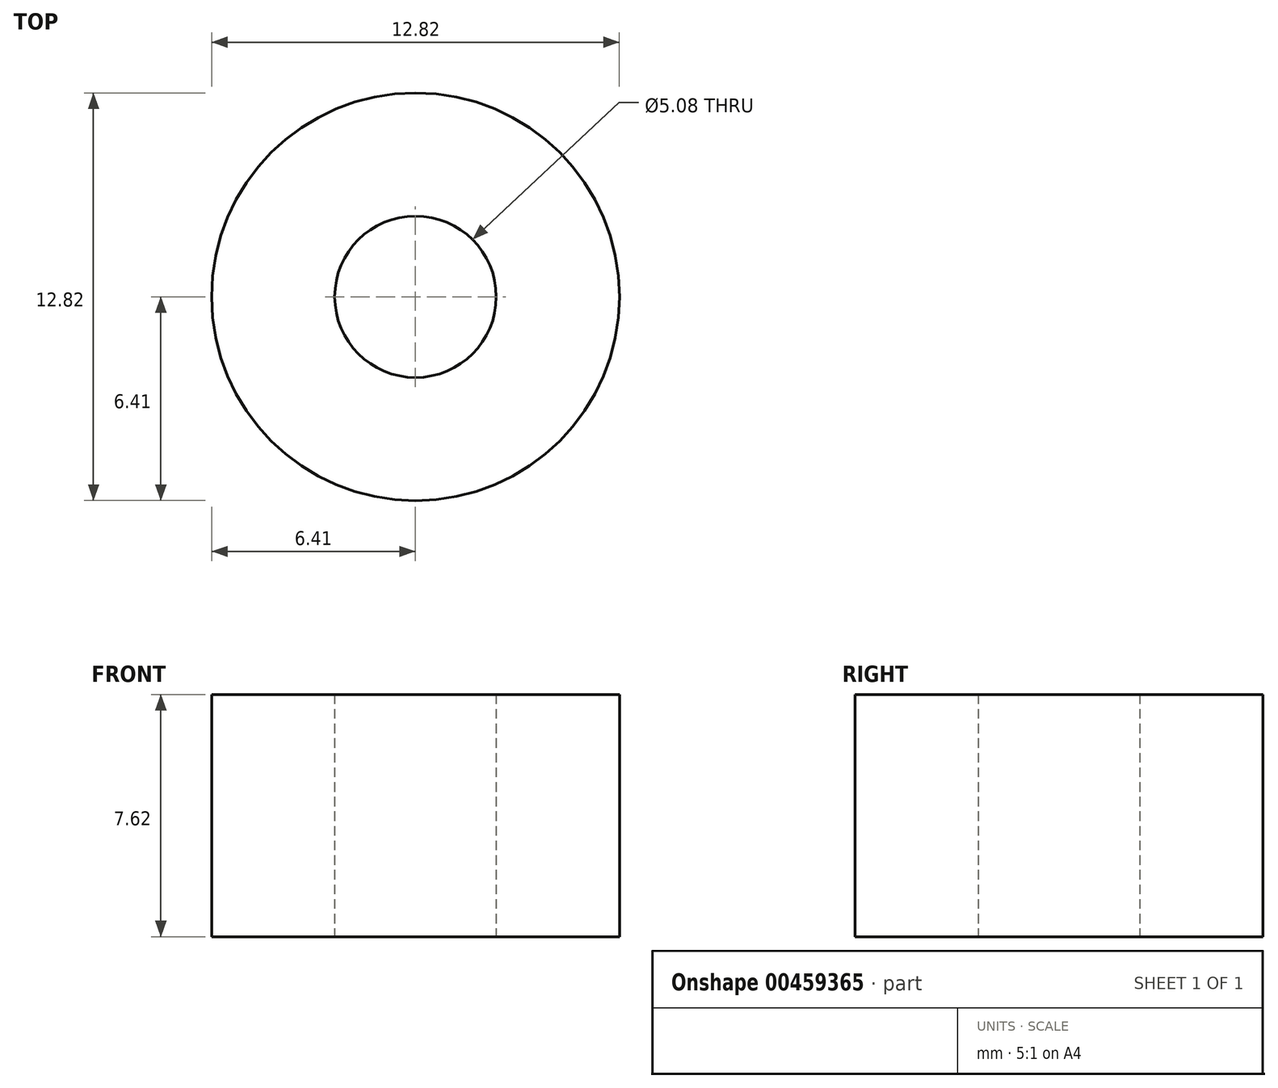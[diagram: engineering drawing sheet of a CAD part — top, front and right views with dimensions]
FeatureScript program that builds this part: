
annotation { "Feature Type Name" : "Feature", "Feature Type Description" : "" }
export const myFeature = defineFeature(function(context is Context, id is Id, definition is map)
    precondition{}
    {
        {
            var Q0;
            Q0=qCreatedBy(makeId("Top.planeOp"),FACE);
            var sketch = newSketch(context, id + "F0", { "sketchPlane" : qUnion([Q0])});
            skCircle(sketch, "E0", {"center": v(0, 0) * mm, "radius": 2.54 * mm});
            skCircle(sketch, "E1", {"center": v(0, 0) * mm, "radius": 6.41 * mm});
            skSolve(sketch);
        }
        {
            var Q0;
            Q0=makeQuery(id+"F0.imprint","IMPRINT",FACE,{"disambiguationData":[TD([[makeQuery(id+"F0.imprint","IMPRINT",EDGE,{"derivedFrom":sQuery(id+"F0.wireOp",EDGE,"E0")}),-1.0]])]});
            extrude(context, id + "F1", {"entities" : qUnion([Q0]), "depth" : 7.62 * mm});
        }
    });
